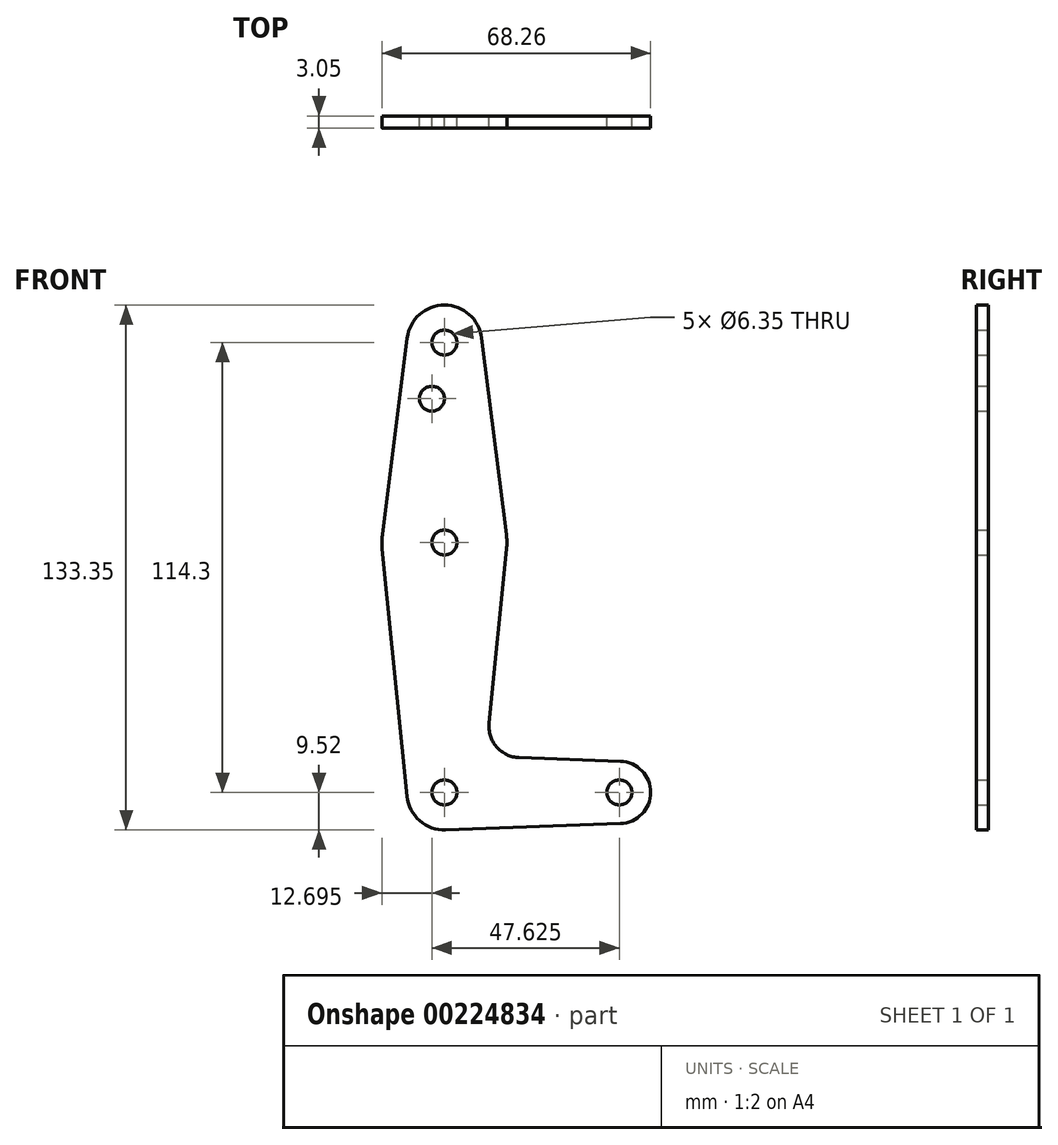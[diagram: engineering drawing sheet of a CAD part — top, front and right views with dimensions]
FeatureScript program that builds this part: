
annotation { "Feature Type Name" : "Feature", "Feature Type Description" : "" }
export const myFeature = defineFeature(function(context is Context, id is Id, definition is map)
    precondition{}
    {
        {
            var Q0;
            Q0=qCreatedBy(makeId("Front.planeOp"),FACE);
            var sketch = newSketch(context, id + "F0", { "sketchPlane" : qUnion([Q0])});
            skLineSegment(sketch, "E0", {"start": v(0, 0) * mm, "end": v(0, 114.3) * mm, "construction": true});
            skLineSegment(sketch, "E1", {"start": v(0, 0) * mm, "end": v(44.45, 0) * mm, "construction": true});
            skCircle(sketch, "E2", {"center": v(0, 0) * mm, "radius": 9.53 * mm});
            skCircle(sketch, "E3", {"center": v(44.45, 0) * mm, "radius": 7.94 * mm});
            skCircle(sketch, "E4", {"center": v(0, 114.3) * mm, "radius": 9.53 * mm});
            skCircle(sketch, "E5", {"center": v(0, 63.5) * mm, "radius": 15.88 * mm});
            skLineSegment(sketch, "E6", {"start": v(-9.45, 115.5) * mm, "end": v(-15.75, 65.48) * mm});
            skLineSegment(sketch, "E7", {"start": v(9.45, 115.5) * mm, "end": v(15.75, 65.48) * mm});
            skLineSegment(sketch, "E8", {"start": v(-15.8, 61.91) * mm, "end": v(-9.48, -0.95) * mm});
            skLineSegment(sketch, "E9", {"start": v(15.8, 61.91) * mm, "end": v(11.34, 17.6) * mm});
            skLineSegment(sketch, "E10", {"start": v(18.97, 8.85) * mm, "end": v(44.73, 7.93) * mm});
            skLineSegment(sketch, "E11", {"start": v(0.34, -9.52) * mm, "end": v(44.73, -7.93) * mm});
            skCircle(sketch, "E12", {"center": v(0, 114.3) * mm, "radius": 3.18 * mm});
            skCircle(sketch, "E13", {"center": v(0, 63.5) * mm, "radius": 3.18 * mm});
            skCircle(sketch, "E14", {"center": v(0, 0) * mm, "radius": 3.18 * mm});
            skCircle(sketch, "E15", {"center": v(44.45, 0) * mm, "radius": 3.18 * mm});
            skCircle(sketch, "E16", {"center": v(-3.17, 100.03) * mm, "radius": 3.18 * mm});
            skArc(sketch, "E17.filletArc", {"start": v(11.34, 17.6) * mm, "mid": v(13.26, 11.57) * mm, "end": v(18.97, 8.85) * mm});
            skSolve(sketch);
        }
        {
            var Q0;
            Q0 = qSketchRegion(id + "F0", true);
            extrude(context, id + "F1", {"entities" : qUnion([Q0]), "depth" : 3.05 * mm});
        }
    });
